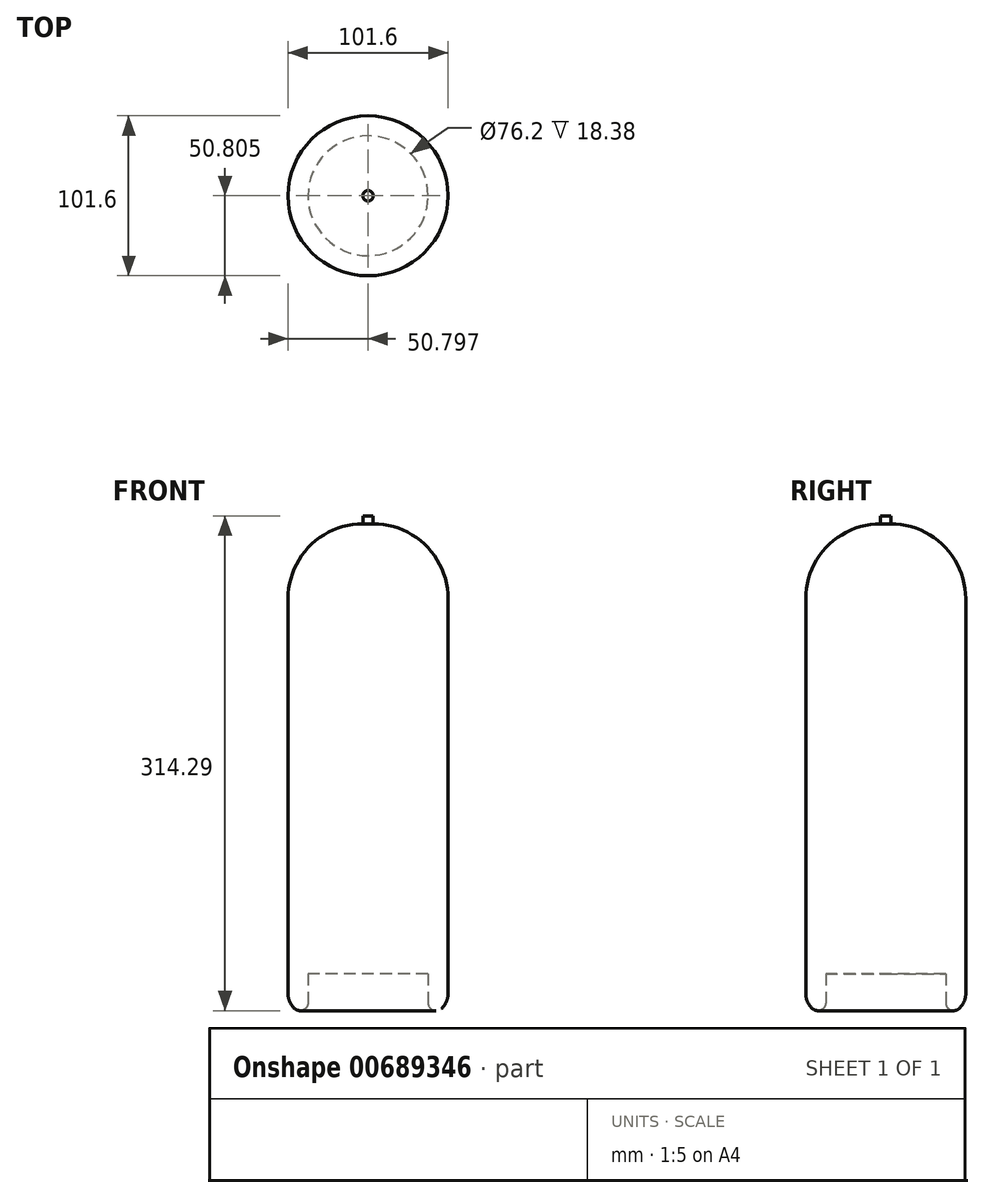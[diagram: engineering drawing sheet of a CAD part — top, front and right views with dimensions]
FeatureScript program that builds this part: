
annotation { "Feature Type Name" : "Feature", "Feature Type Description" : "" }
export const myFeature = defineFeature(function(context is Context, id is Id, definition is map)
    precondition{}
    {
        {
            var Q0;
            Q0=qCreatedBy(makeId("Top.planeOp"),FACE);
            var sketch = newSketch(context, id + "F0", { "sketchPlane" : qUnion([Q0])});
            skCircle(sketch, "E0", {"center": v(-30.63, 40.14) * mm, "radius": 50.8 * mm});
            skSolve(sketch);
        }
        {
            var Q0;
            Q0 = qSketchRegion(id + "F0", true);
            extrude(context, id + "F1", {"entities" : qUnion([Q0]), "depth" : 311.15 * mm, "offsetDistance" : 25.4 * mm});
        }
        {
            var Q0;
            Q0=makeQuery(id+"F1.opExtrude","CAP_EDGE",EDGE,{"disambiguationData":[OSD([sQuery(id+"F0.wireOp",EDGE,"E0")])],"isStart":false});
            fillet(context, id + "F2", {"entities" : qUnion([Q0]), "radius" : 47.5 * mm, "tangentPropagation" : true, "allowEdgeOverflow" : false});
        }
        {
            var Q0;
            Q0=makeQuery(id+"F1.opExtrude","CAP_FACE",FACE,{"disambiguationData":[OSD([sQuery(id+"F0.wireOp",EDGE,"E0")])],"isStart":false});
            extrude(context, id + "F3", {"entities" : qUnion([Q0]), "operationType" : NewBodyOperationType.ADD, "depth" : 5.08 * mm, "offsetDistance" : 25.4 * mm});
        }
        {
            var Q0;
            Q0=makeQuery(id+"F1.opExtrude","CAP_EDGE",EDGE,{"disambiguationData":[OSD([sQuery(id+"F0.wireOp",EDGE,"E0")])],"isStart":true});
            fillet(context, id + "F4", {"entities" : qUnion([Q0]), "radius" : 12.7 * mm, "tangentPropagation" : true, "allowEdgeOverflow" : false});
        }
        {
            var Q0;
            Q0=makeQuery(id+"F1.opExtrude","CAP_FACE",FACE,{"disambiguationData":[OSD([sQuery(id+"F0.wireOp",EDGE,"E0")])],"isStart":true});
            extrude(context, id + "F5", {"entities" : qUnion([Q0]), "operationType" : NewBodyOperationType.REMOVE, "oppositeDirection" : true, "depth" : 25.4 * mm, "offsetDistance" : 25.4 * mm});
        }
        {
            var Q0;
            {var subQ0=sQuery(id+"F0.wireOp",EDGE,"E0");Q0=makeQuery(id+"F5.boolean.opBoolean","MERGE",EDGE,{"derivedFrom":[makeQuery(id+"F4.opFillet","BLEND_EDGE",EDGE,{"blendedFrom":[makeQuery(id+"F1.opExtrude","CAP_EDGE",EDGE,{"disambiguationData":[OSD([subQ0])],"isStart":true}),makeQuery(id+"F1.opExtrude","CAP_FACE",FACE,{"disambiguationData":[OSD([subQ0])],"isStart":true})],"blendedInto":[makeQuery(id+"F1.opExtrude","CAP_FACE",FACE,{"disambiguationData":[OSD([subQ0])],"isStart":true})]}),makeQuery(id+"F5.opExtrude","CAP_EDGE",EDGE,{"disambiguationData":[OSD([subQ0])],"isStart":true})]});}
            fillet(context, id + "F6", {"entities" : qUnion([Q0]), "radius" : 5.08 * mm, "tangentPropagation" : true, "allowEdgeOverflow" : false});
        }
    });
